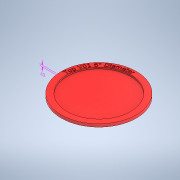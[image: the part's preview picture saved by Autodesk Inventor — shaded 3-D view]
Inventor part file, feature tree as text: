
AUTODESK INVENTOR PART (.ipt)
format: ipt  version: 2021.1 (Build 251245010, 245A)  size: 518,656 bytes
history: native  units: in
note: dims shown in document units (in); Inventor stores cm internally (conversion verified against a paired STEP export)
features: sketch x3, other x2, extrude x2, revolve x1
ambient origin geometry x8: Origin, YZ Plane, XZ Plane, XY Plane, X Axis, Y Axis, Z Axis, Center Point
bodies: Body1 (feature_tree)
feature tree (8):
  other  "Annotations"
  revolve  "Revolution3"  [1 undecoded]
  extrude  "Extrusion3"  TaperAngle=90.0deg  [1 undecoded]
  extrude  "Extrusion4"  Depth=0.125in TaperAngle=0.0deg
  sketch  "Sketch6"  dims[d25=0.5in d26=0.125in]
  sketch  "Sketch7"  dims[d27=2.75in d28=90.0deg]
  sketch  "Sketch8"  dims[d29=6.0in d30=0.05in d31=0.0in d35=0.125in d36=0.0in d32=0.218in d33=0.0211in d34=0.125in]
  other  "Linear Dimension 1"
note: 2 required parameter values undecoded (feature->parameter linkage not recoverable at this tier; creation-order binding heuristic only, values carry confidence <= 0.55)